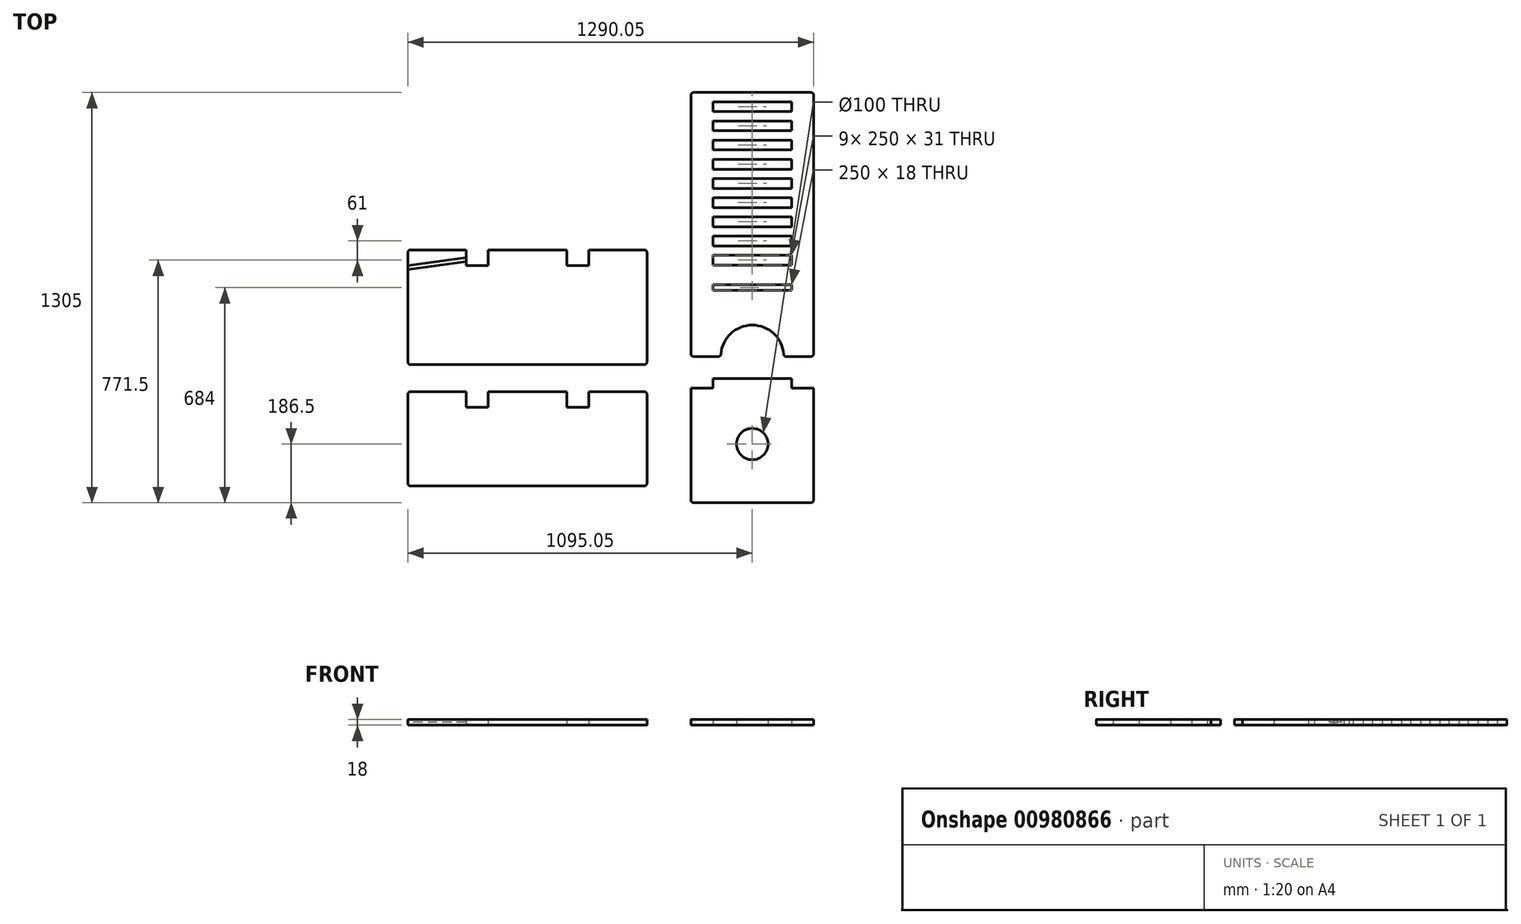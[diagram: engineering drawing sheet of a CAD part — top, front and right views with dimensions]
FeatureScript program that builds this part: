
annotation { "Feature Type Name" : "Feature", "Feature Type Description" : "" }
export const myFeature = defineFeature(function(context is Context, id is Id, definition is map)
    precondition{}
    {
        {
            assignVariable(context, id + "F0", {"name" : "MaterialThickness", "anyValue" : 18 * mm});
        }
        {
            var Q0;
            Q0=qCreatedBy(makeId("Top.planeOp"),FACE);
            var sketch = newSketch(context, id + "F1", { "sketchPlane" : qUnion([Q0])});
            skLineSegment(sketch, "E0.bottom", {"start": v(-187, 0) * mm, "end": v(-107.7, 0) * mm});
            skLineSegment(sketch, "E0.top", {"start": v(-187, 840) * mm, "end": v(187, 840) * mm});
            skLineSegment(sketch, "E0.left", {"start": v(-195, 8) * mm, "end": v(-195, 832) * mm});
            skLineSegment(sketch, "E0.right", {"start": v(195, 8) * mm, "end": v(195, 832) * mm});
            skLineSegment(sketch, "E1", {"start": v(0, -93.61) * mm, "end": v(0, 881.1) * mm, "construction": true});
            skLineSegment(sketch, "E2.bottom", {"start": v(-125, 228) * mm, "end": v(125, 228) * mm});
            skLineSegment(sketch, "E2.top", {"start": v(-125, 210) * mm, "end": v(125, 210) * mm});
            skLineSegment(sketch, "E2.left", {"start": v(-125, 228) * mm, "end": v(-125, 210) * mm});
            skLineSegment(sketch, "E2.right", {"start": v(125, 228) * mm, "end": v(125, 210) * mm});
            skLineSegment(sketch, "E3", {"start": v(-273.2, 794.5) * mm, "end": v(273.2, 794.5) * mm, "construction": true});
            skLineSegment(sketch, "E4.bottom", {"start": v(-125, 810) * mm, "end": v(125, 810) * mm});
            skLineSegment(sketch, "E4.top", {"start": v(-125, 779) * mm, "end": v(125, 779) * mm});
            skLineSegment(sketch, "E4.left", {"start": v(-125, 810) * mm, "end": v(-125, 779) * mm});
            skLineSegment(sketch, "E4.right", {"start": v(125, 810) * mm, "end": v(125, 779) * mm});
            skPoint(sketch, "E4.middle", {"position": v(0, 794.5) * mm});
            skLineSegment(sketch, "E5.0.1.0", {"start": v(-125, 749) * mm, "end": v(-125, 718) * mm});
            skLineSegment(sketch, "E5.0.1.1", {"start": v(-125, 749) * mm, "end": v(125, 749) * mm});
            skLineSegment(sketch, "E5.0.1.2", {"start": v(125, 749) * mm, "end": v(125, 718) * mm});
            skLineSegment(sketch, "E5.0.1.3", {"start": v(-125, 718) * mm, "end": v(125, 718) * mm});
            skLineSegment(sketch, "E5.0.2.0", {"start": v(-125, 688) * mm, "end": v(-125, 657) * mm});
            skLineSegment(sketch, "E5.0.2.1", {"start": v(-125, 688) * mm, "end": v(125, 688) * mm});
            skLineSegment(sketch, "E5.0.2.2", {"start": v(125, 688) * mm, "end": v(125, 657) * mm});
            skLineSegment(sketch, "E5.0.2.3", {"start": v(-125, 657) * mm, "end": v(125, 657) * mm});
            skLineSegment(sketch, "E5.0.3.0", {"start": v(-125, 627) * mm, "end": v(-125, 596) * mm});
            skLineSegment(sketch, "E5.0.3.1", {"start": v(-125, 627) * mm, "end": v(125, 627) * mm});
            skLineSegment(sketch, "E5.0.3.2", {"start": v(125, 627) * mm, "end": v(125, 596) * mm});
            skLineSegment(sketch, "E5.0.3.3", {"start": v(-125, 596) * mm, "end": v(125, 596) * mm});
            skLineSegment(sketch, "E5.0.4.0", {"start": v(-125, 566) * mm, "end": v(-125, 535) * mm});
            skLineSegment(sketch, "E5.0.4.1", {"start": v(-125, 566) * mm, "end": v(125, 566) * mm});
            skLineSegment(sketch, "E5.0.4.2", {"start": v(125, 566) * mm, "end": v(125, 535) * mm});
            skLineSegment(sketch, "E5.0.4.3", {"start": v(-125, 535) * mm, "end": v(125, 535) * mm});
            skLineSegment(sketch, "E5.0.5.0", {"start": v(-125, 505) * mm, "end": v(-125, 474) * mm});
            skLineSegment(sketch, "E5.0.5.1", {"start": v(-125, 505) * mm, "end": v(125, 505) * mm});
            skLineSegment(sketch, "E5.0.5.2", {"start": v(125, 505) * mm, "end": v(125, 474) * mm});
            skLineSegment(sketch, "E5.0.5.3", {"start": v(-125, 474) * mm, "end": v(125, 474) * mm});
            skLineSegment(sketch, "E5.0.6.0", {"start": v(-125, 444) * mm, "end": v(-125, 413) * mm});
            skLineSegment(sketch, "E5.0.6.1", {"start": v(-125, 444) * mm, "end": v(125, 444) * mm});
            skLineSegment(sketch, "E5.0.6.2", {"start": v(125, 444) * mm, "end": v(125, 413) * mm});
            skLineSegment(sketch, "E5.0.6.3", {"start": v(-125, 413) * mm, "end": v(125, 413) * mm});
            skLineSegment(sketch, "E5.0.7.0", {"start": v(-125, 383) * mm, "end": v(-125, 352) * mm});
            skLineSegment(sketch, "E5.0.7.1", {"start": v(-125, 383) * mm, "end": v(125, 383) * mm});
            skLineSegment(sketch, "E5.0.7.2", {"start": v(125, 383) * mm, "end": v(125, 352) * mm});
            skLineSegment(sketch, "E5.0.7.3", {"start": v(-125, 352) * mm, "end": v(125, 352) * mm});
            skLineSegment(sketch, "E5.0.8.0", {"start": v(-125, 322) * mm, "end": v(-125, 291) * mm});
            skLineSegment(sketch, "E5.0.8.1", {"start": v(-125, 322) * mm, "end": v(125, 322) * mm});
            skLineSegment(sketch, "E5.0.8.2", {"start": v(125, 322) * mm, "end": v(125, 291) * mm});
            skLineSegment(sketch, "E5.0.8.3", {"start": v(-125, 291) * mm, "end": v(125, 291) * mm});
            skLineSegment(sketch, "E5.direction1", {"start": v(-125, 779) * mm, "end": v(-100, 779) * mm, "construction": true});
            skLineSegment(sketch, "E5.direction2", {"start": v(-125, 779) * mm, "end": v(-125, 718) * mm, "construction": true});
            skPoint(sketch, "E6.visualSharp", {"position": v(-195, 840) * mm});
            skArc(sketch, "E6.filletArc", {"start": v(-187, 840) * mm, "mid": v(-192.66, 837.66) * mm, "end": v(-195, 832) * mm});
            skPoint(sketch, "E7.visualSharp", {"position": v(195, 840) * mm});
            skArc(sketch, "E7.filletArc", {"start": v(195, 832) * mm, "mid": v(192.66, 837.66) * mm, "end": v(187, 840) * mm});
            skPoint(sketch, "E8.visualSharp", {"position": v(-195, 0) * mm});
            skArc(sketch, "E8.filletArc", {"start": v(-195, 8) * mm, "mid": v(-192.66, 2.34) * mm, "end": v(-187, 0) * mm});
            skPoint(sketch, "E9.visualSharp", {"position": v(195, 0) * mm});
            skArc(sketch, "E9.filletArc", {"start": v(187, 0) * mm, "mid": v(192.66, 2.34) * mm, "end": v(195, 8) * mm});
            skArc(sketch, "E10", {"start": v(-99.73, 7.4) * mm, "mid": v(0, 100) * mm, "end": v(99.73, 7.4) * mm});
            skLineSegment(sketch, "E11.trimOffspring", {"start": v(107.7, 0) * mm, "end": v(187, 0) * mm});
            skPoint(sketch, "E12.visualSharp", {"position": v(-100, 0) * mm});
            skArc(sketch, "E12.filletArc", {"start": v(-107.7, 0) * mm, "mid": v(-102.26, 2.14) * mm, "end": v(-99.73, 7.4) * mm});
            skPoint(sketch, "E13.visualSharp", {"position": v(100, 0) * mm});
            skArc(sketch, "E13.filletArc", {"start": v(99.73, 7.4) * mm, "mid": v(102.26, 2.14) * mm, "end": v(107.7, 0) * mm});
            skSolve(sketch);
        }
        {
            var Q0;
            Q0=makeQuery(id+"F1.imprint","IMPRINT",FACE,{"disambiguationData":[TD([[makeQuery(id+"F1.imprint","IMPRINT",EDGE,{"derivedFrom":sQuery(id+"F1.wireOp",EDGE,"E0.bottom")}),1.0]])]});
            extrude(context, id + "F2", {"entities" : qUnion([Q0]), "depth" : getVariable(context, 'MaterialThickness'), "offsetDistance" : 25 * mm});
        }
        {
            var Q0;
            Q0=qCreatedBy(makeId("Top.planeOp"),FACE);
            var sketch = newSketch(context, id + "F3", { "sketchPlane" : qUnion([Q0])});
            skLineSegment(sketch, "E14.bottom", {"start": v(-125, -70) * mm, "end": v(125, -70) * mm});
            skLineSegment(sketch, "E14.top", {"start": v(-187, -465) * mm, "end": v(187, -465) * mm});
            skLineSegment(sketch, "E14.left", {"start": v(-195, -100) * mm, "end": v(-195, -457) * mm});
            skLineSegment(sketch, "E14.right", {"start": v(195, -100) * mm, "end": v(195, -457) * mm});
            skLineSegment(sketch, "E15", {"start": v(0, 94.42) * mm, "end": v(0, -77.08) * mm, "construction": true});
            skLineSegment(sketch, "E16", {"start": v(-125, -70) * mm, "end": v(-125, -100) * mm});
            skLineSegment(sketch, "E17", {"start": v(-125, -100) * mm, "end": v(-195, -100) * mm});
            skLineSegment(sketch, "E18", {"start": v(125, -70) * mm, "end": v(125, -100) * mm});
            skLineSegment(sketch, "E19", {"start": v(125, -100) * mm, "end": v(195, -100) * mm});
            skPoint(sketch, "E20.visualSharp", {"position": v(-195, -465) * mm});
            skArc(sketch, "E20.filletArc", {"start": v(-195, -457) * mm, "mid": v(-192.66, -462.66) * mm, "end": v(-187, -465) * mm});
            skPoint(sketch, "E21.visualSharp", {"position": v(195, -465) * mm});
            skArc(sketch, "E21.filletArc", {"start": v(187, -465) * mm, "mid": v(192.66, -462.66) * mm, "end": v(195, -457) * mm});
            skCircle(sketch, "E22", {"center": v(0, -278.5) * mm, "radius": 50 * mm});
            skPoint(sketch, "E22.centerSnap0", {"position": v(-195, -278.5) * mm});
            skSolve(sketch);
        }
        {
            var Q0;
            Q0 = qSketchRegion(id + "F3", true);
            extrude(context, id + "F4", {"entities" : qUnion([Q0]), "depth" : getVariable(context, 'MaterialThickness'), "offsetDistance" : 25 * mm});
        }
        {
            var Q0;
            Q0=qCreatedBy(makeId("Top.planeOp"),FACE);
            var sketch = newSketch(context, id + "F5", { "sketchPlane" : qUnion([Q0])});
            skLineSegment(sketch, "E23.bottom", {"start": v(-1087.05, 339.27) * mm, "end": v(-910.05, 339.27) * mm});
            skLineSegment(sketch, "E23.top", {"start": v(-1087.05, -25.73) * mm, "end": v(-343.05, -25.73) * mm});
            skLineSegment(sketch, "E23.left", {"start": v(-1095.05, 331.27) * mm, "end": v(-1095.05, -17.73) * mm});
            skLineSegment(sketch, "E23.right", {"start": v(-335.05, 331.27) * mm, "end": v(-335.05, -17.73) * mm});
            skLineSegment(sketch, "E24", {"start": v(-910.05, 289.27) * mm, "end": v(-840.05, 289.27) * mm});
            skLineSegment(sketch, "E25", {"start": v(-910.05, 339.27) * mm, "end": v(-910.05, 289.27) * mm});
            skLineSegment(sketch, "E26", {"start": v(-840.05, 339.27) * mm, "end": v(-840.05, 289.27) * mm});
            skLineSegment(sketch, "E27", {"start": v(-590.05, 339.27) * mm, "end": v(-590.05, 289.27) * mm});
            skLineSegment(sketch, "E28", {"start": v(-520.05, 339.27) * mm, "end": v(-520.05, 289.27) * mm});
            skLineSegment(sketch, "E29.trimOffspring", {"start": v(-520.05, 339.27) * mm, "end": v(-343.05, 339.27) * mm});
            skLineSegment(sketch, "E30.trimOffspring", {"start": v(-840.05, 339.27) * mm, "end": v(-590.05, 339.27) * mm});
            skLineSegment(sketch, "E31.trimOffspring", {"start": v(-590.05, 289.27) * mm, "end": v(-520.05, 289.27) * mm});
            skLineSegment(sketch, "E32", {"start": v(-715.05, -42.22) * mm, "end": v(-715.05, 420.46) * mm, "construction": true});
            skPoint(sketch, "E32.startSnap0", {"position": v(-715.05, -25.73) * mm});
            skPoint(sketch, "E33.visualSharp", {"position": v(-1095.05, -25.73) * mm});
            skArc(sketch, "E33.filletArc", {"start": v(-1095.05, -17.73) * mm, "mid": v(-1092.71, -23.38) * mm, "end": v(-1087.05, -25.73) * mm});
            skPoint(sketch, "E34.visualSharp", {"position": v(-335.05, -25.73) * mm});
            skArc(sketch, "E34.filletArc", {"start": v(-343.05, -25.73) * mm, "mid": v(-337.4, -23.38) * mm, "end": v(-335.05, -17.73) * mm});
            skPoint(sketch, "E35.visualSharp", {"position": v(-335.05, 339.27) * mm});
            skArc(sketch, "E35.filletArc", {"start": v(-335.05, 331.27) * mm, "mid": v(-337.4, 336.93) * mm, "end": v(-343.05, 339.27) * mm});
            skPoint(sketch, "E36.visualSharp", {"position": v(-1095.05, 339.27) * mm});
            skArc(sketch, "E36.filletArc", {"start": v(-1087.05, 339.27) * mm, "mid": v(-1092.71, 336.93) * mm, "end": v(-1095.05, 331.27) * mm});
            skSolve(sketch);
        }
        {
            var Q0;
            Q0=makeQuery(id+"F5.imprint","IMPRINT",FACE,{"disambiguationData":[TD([[makeQuery(id+"F5.imprint","IMPRINT",EDGE,{"derivedFrom":sQuery(id+"F5.wireOp",EDGE,"E23.bottom")}),-1.0]])]});
            extrude(context, id + "F6", {"entities" : qUnion([Q0]), "depth" : getVariable(context, 'MaterialThickness'), "offsetDistance" : 25 * mm});
        }
        {
            var Q0;
            Q0=makeQuery(id+"F6.opExtrude","CAP_FACE",FACE,{"disambiguationData":[OSD([sQuery(id+"F5.wireOp",EDGE,"E23.bottom"),sQuery(id+"F5.wireOp",EDGE,"E23.top"),sQuery(id+"F5.wireOp",EDGE,"E23.left"),sQuery(id+"F5.wireOp",EDGE,"E23.right"),sQuery(id+"F5.wireOp",EDGE,"E24"),sQuery(id+"F5.wireOp",EDGE,"E25"),sQuery(id+"F5.wireOp",EDGE,"E26"),sQuery(id+"F5.wireOp",EDGE,"E27"),sQuery(id+"F5.wireOp",EDGE,"E28"),sQuery(id+"F5.wireOp",EDGE,"E29.trimOffspring"),sQuery(id+"F5.wireOp",EDGE,"E30.trimOffspring"),sQuery(id+"F5.wireOp",EDGE,"E31.trimOffspring"),sQuery(id+"F5.wireOp",EDGE,"E33.filletArc"),sQuery(id+"F5.wireOp",EDGE,"E34.filletArc"),sQuery(id+"F5.wireOp",EDGE,"E35.filletArc"),sQuery(id+"F5.wireOp",EDGE,"E36.filletArc")])],"isStart":false});
            var sketch = newSketch(context, id + "F7", { "sketchPlane" : qUnion([Q0])});
            skLineSegment(sketch, "E37", {"start": v(-910.05, 314.27) * mm, "end": v(-1095.05, 289.27) * mm});
            skLineSegment(sketch, "E38", {"start": v(-1095.05, 289.27) * mm, "end": v(-1095.05, 277.16) * mm});
            skLineSegment(sketch, "E39", {"start": v(-1095.05, 277.16) * mm, "end": v(-910.05, 302.16) * mm});
            skLineSegment(sketch, "E40", {"start": v(-910.05, 302.16) * mm, "end": v(-910.05, 314.27) * mm});
            skSolve(sketch);
        }
        {
            var Q0;
            Q0=makeQuery(id+"F7.imprint","IMPRINT",FACE,{"disambiguationData":[TD([[makeQuery(id+"F7.imprint","IMPRINT",EDGE,{"derivedFrom":sQuery(id+"F7.wireOp",EDGE,"E37")}),1.0]])]});
            extrude(context, id + "F8", {"entities" : qUnion([Q0]), "operationType" : NewBodyOperationType.REMOVE, "oppositeDirection" : true, "depth" : 9 * mm, "offsetDistance" : 25 * mm});
        }
        {
            var Q0;
            Q0=qCreatedBy(makeId("Top.planeOp"),FACE);
            var Q1;
            {var subQ0=sQuery(id+"F5.wireOp",EDGE,"E30.trimOffspring");var subQ1=sQuery(id+"F5.wireOp",EDGE,"E29.trimOffspring");var subQ2=sQuery(id+"F5.wireOp",EDGE,"E28");var subQ3=sQuery(id+"F5.wireOp",EDGE,"E27");var subQ4=sQuery(id+"F5.wireOp",EDGE,"E26");var subQ5=sQuery(id+"F5.wireOp",EDGE,"E25");var subQ6=sQuery(id+"F5.wireOp",EDGE,"E23.top");var subQ7=sQuery(id+"F5.wireOp",EDGE,"E23.left");var subQ8=sQuery(id+"F5.wireOp",EDGE,"E23.right");var subQ9=sQuery(id+"F5.wireOp",EDGE,"E24");var subQ10=sQuery(id+"F5.wireOp",EDGE,"E31.trimOffspring");var subQ11=sQuery(id+"F5.wireOp",EDGE,"E33.filletArc");var subQ12=sQuery(id+"F5.wireOp",EDGE,"E34.filletArc");var subQ13=sQuery(id+"F5.wireOp",EDGE,"E35.filletArc");Q1=makeQuery(id+"F8.boolean.opBoolean","SPLIT",FACE,{"disambiguationData":[TD([makeQuery(id+"F6.opExtrude","SWEPT_FACE",FACE,{"disambiguationData":[OSD([subQ6])]})])],"derivedFrom":makeQuery(id+"F6.opExtrude","CAP_FACE",FACE,{"disambiguationData":[OSD([sQuery(id+"F5.wireOp",EDGE,"E23.bottom"),subQ6,subQ7,subQ8,subQ9,subQ5,subQ4,subQ3,subQ2,subQ1,subQ0,subQ10,subQ11,subQ12,subQ13,sQuery(id+"F5.wireOp",EDGE,"E36.filletArc")])],"isStart":false})});}
            var sketch = newSketch(context, id + "F9", { "sketchPlane" : qUnion([Q0, Q1])});
            skLineSegment(sketch, "E41.bottom", {"start": v(-1087.05, -112.03) * mm, "end": v(-910.05, -112.03) * mm});
            skLineSegment(sketch, "E41.top", {"start": v(-1087.05, -412.03) * mm, "end": v(-343.05, -412.03) * mm});
            skLineSegment(sketch, "E41.left", {"start": v(-1095.05, -120.03) * mm, "end": v(-1095.05, -404.03) * mm});
            skLineSegment(sketch, "E41.right", {"start": v(-335.05, -120.03) * mm, "end": v(-335.05, -404.03) * mm});
            skLineSegment(sketch, "E42", {"start": v(-910.05, -162.03) * mm, "end": v(-840.05, -162.03) * mm});
            skLineSegment(sketch, "E43", {"start": v(-910.05, -112.03) * mm, "end": v(-910.05, -162.03) * mm});
            skLineSegment(sketch, "E44", {"start": v(-840.05, -112.03) * mm, "end": v(-840.05, -162.03) * mm});
            skLineSegment(sketch, "E45", {"start": v(-590.05, -112.03) * mm, "end": v(-590.05, -162.03) * mm});
            skLineSegment(sketch, "E46", {"start": v(-520.05, -112.03) * mm, "end": v(-520.05, -162.03) * mm});
            skLineSegment(sketch, "E47.trimOffspring", {"start": v(-520.05, -112.03) * mm, "end": v(-343.05, -112.03) * mm});
            skLineSegment(sketch, "E48.trimOffspring", {"start": v(-840.05, -112.03) * mm, "end": v(-590.05, -112.03) * mm});
            skLineSegment(sketch, "E49.trimOffspring", {"start": v(-590.05, -162.03) * mm, "end": v(-520.05, -162.03) * mm});
            skLineSegment(sketch, "E50", {"start": v(-715.05, -504.9) * mm, "end": v(-715.05, -42.22) * mm, "construction": true});
            skPoint(sketch, "E50.startSnap0", {"position": v(-715.05, -412.03) * mm});
            skPoint(sketch, "E51.visualSharp", {"position": v(-1095.05, -412.03) * mm});
            skArc(sketch, "E51.filletArc", {"start": v(-1095.05, -404.03) * mm, "mid": v(-1092.71, -409.68) * mm, "end": v(-1087.05, -412.03) * mm});
            skPoint(sketch, "E52.visualSharp", {"position": v(-335.05, -412.03) * mm});
            skArc(sketch, "E52.filletArc", {"start": v(-343.05, -412.03) * mm, "mid": v(-337.4, -409.68) * mm, "end": v(-335.05, -404.03) * mm});
            skPoint(sketch, "E53.visualSharp", {"position": v(-335.05, -112.03) * mm});
            skArc(sketch, "E53.filletArc", {"start": v(-335.05, -120.03) * mm, "mid": v(-337.4, -114.37) * mm, "end": v(-343.05, -112.03) * mm});
            skPoint(sketch, "E54.visualSharp", {"position": v(-1095.05, -112.03) * mm});
            skArc(sketch, "E54.filletArc", {"start": v(-1087.05, -112.03) * mm, "mid": v(-1092.71, -114.37) * mm, "end": v(-1095.05, -120.03) * mm});
            skSolve(sketch);
        }
        {
            var Q0;
            Q0 = qSketchRegion(id + "F9", true);
            extrude(context, id + "F10", {"entities" : qUnion([Q0]), "depth" : 18 * mm, "offsetDistance" : 25 * mm});
        }
    });
